# Revit family: Sink-Bradley_Corp-Verge-LVGD2
name_source: partatom
category: Plumbing Fixtures
revit_build: Autodesk Revit MEP 2012 (Build: 20110309_2315(x64)
units: mm (PartAtom-declared; Revit-internal decimal feet)

## types (4) — shared parameters
Access Panel Material = Metal - Bradley Corp - Stainless Steel
Apparent Load = 0 VA
Assembly Code = D2010400
CWFU = 0.5
Cold Water Connection Diameter = 0.5 "
Cold Water Connection Radius = 0.25 "
Depth = 22.5 "
Description = Verge™ Lavatory System – LVRD-Series, Two-Station
Evero™ Bowl Material = Stone - Bradley Corp - Zanzibar
Fixture Material = Metal - Bradley Corp - Chrome
HWFU = 0.5
Hot Water Connection Diameter = 0.5 "
Hot Water Connection Radius = 0.25 "
Installation Type = Wall Mounted
Low Emitting Material = Yes
Manufacturer = Bradley Corporation
MasterFormat Number = 22 42 16
MasterFormat Title = Commercial Lavatories and Sinks
Material = Polyester Resin
Material Note = Other Evero™ colors available - See www.bradleycorp.com
Model = LVGD2
Number of Poles = 1
OmniClass Table 21 Number = 21-04 20 10 60
OmniClass Table 21 Title = Plumbing Fixtures
OmniClass Table 23 Number = 23-31 13 00
OmniClass Table 23 Title = Sink/Lavatories
Pedestal Width = 36 "
Power Factor = 1
Product Tech Data URL - English = http://bradleycorp.com
Specifications URL = http://www.bradleycorp.com
URL = http://www.bradleycorp.com
Version = 3.0
Voltage = 110 V
WFU = 1.5
Waste Connection Diameter = 1.5 "
Waste Connection Radius = 0.75 "
Width = 60.875 "
zero-valued in all types: Percentage of Recycled Content

## per-type parameters (varying)
| type | ADA Compliant | Height | Industry Standards |
| Standard | Yes | 36.375 " | ANSI Z124.3, ANSI Z124.6, ANSI/OCPA SS-1-2001, UPC, GREENGUARD Indoor Air Quality Certified®, GREENGUARD Children & Schools(SM) |
| Juvenile Height | Yes | 33.375 " | ANSI Z124.3, ANSI Z124.6, ANSI/OCPA SS-1-2001, UPC, GREENGUARD Indoor Air Quality Certified®, GREENGUARD Children & Schools(SM) |
| TAS Grades 6 thru 8 or 9 | No | 34.375 " | TAS, ANSI Z124.3, ANSI Z124.6, ANSI/OCPA SS-1-2001, UPC, GREENGUARD Indoor Air Quality Certified®, GREENGUARD Children & Schools(SM) |
| TAS Pre-K Grades 5 or 6 | No | 32.375 " | TAS, ANSI Z124.3, ANSI Z124.6, ANSI/OCPA SS-1-2001, UPC, GREENGUARD Indoor Air Quality Certified®, GREENGUARD Children & Schools(SM) |

## geometry (parser evidence)
native form markers: Blend x12, Sweep x2
no freeform markers — native parametric forms only
